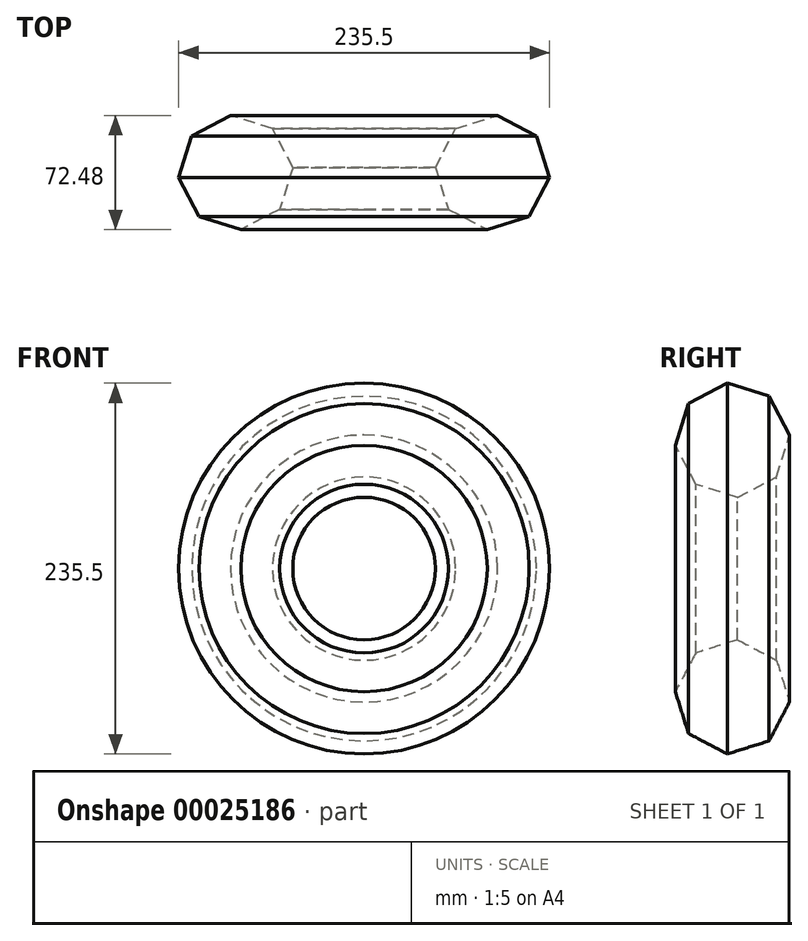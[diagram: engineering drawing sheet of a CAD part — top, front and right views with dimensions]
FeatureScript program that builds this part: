
annotation { "Feature Type Name" : "Feature", "Feature Type Description" : "" }
export const myFeature = defineFeature(function(context is Context, id is Id, definition is map)
    precondition{}
    {
        {
            var Q0;
            Q0=qCreatedBy(makeId("Top.planeOp"),FACE);
            var sketch = newSketch(context, id + "F0", { "sketchPlane" : qUnion([Q0])});
            skLineSegment(sketch, "E0", {"start": v(0, 0) * mm, "end": v(0, 34.33) * mm});
            skSolve(sketch);
        }
        {
            var Q0;
            Q0=qCreatedBy(makeId("Top.planeOp"),FACE);
            var sketch = newSketch(context, id + "F1", { "sketchPlane" : qUnion([Q0])});
            skCircle(sketch, "E1.cCircle", {"center": v(81.51, 0) * mm, "radius": 36.4 * mm, "construction": true});
            skLineSegment(sketch, "E1.0", {"start": v(104.82, -27.95) * mm, "end": v(78.23, -36.24) * mm});
            skLineSegment(sketch, "E1.1", {"start": v(78.23, -36.24) * mm, "end": v(53.56, -23.3) * mm});
            skLineSegment(sketch, "E1.2", {"start": v(53.56, -23.3) * mm, "end": v(45.27, 3.28) * mm});
            skLineSegment(sketch, "E1.3", {"start": v(45.27, 3.28) * mm, "end": v(58.2, 27.95) * mm});
            skLineSegment(sketch, "E1.4", {"start": v(58.2, 27.95) * mm, "end": v(84.8, 36.24) * mm});
            skLineSegment(sketch, "E1.5", {"start": v(84.8, 36.24) * mm, "end": v(109.46, 23.3) * mm});
            skLineSegment(sketch, "E1.6", {"start": v(109.46, 23.3) * mm, "end": v(117.75, -3.28) * mm});
            skLineSegment(sketch, "E1.7", {"start": v(117.75, -3.28) * mm, "end": v(104.82, -27.95) * mm});
            skSolve(sketch);
        }
        {
            var Q0;
            Q0=makeQuery(id+"F1.imprint","IMPRINT",FACE,{"disambiguationData":[TD([[makeQuery(id+"F1.imprint","IMPRINT",EDGE,{"derivedFrom":sQuery(id+"F1.wireOp",EDGE,"E1.0")}),-1.0]])]});
            var Q1;
            Q1=sQuery(id+"F0.wireOp",EDGE,"E0");
            revolve(context, id + "F2", {"entities" : qUnion([Q0]), "axis" : qUnion([Q1]), "revolveType" : RevolveType.FULL});
        }
    });
